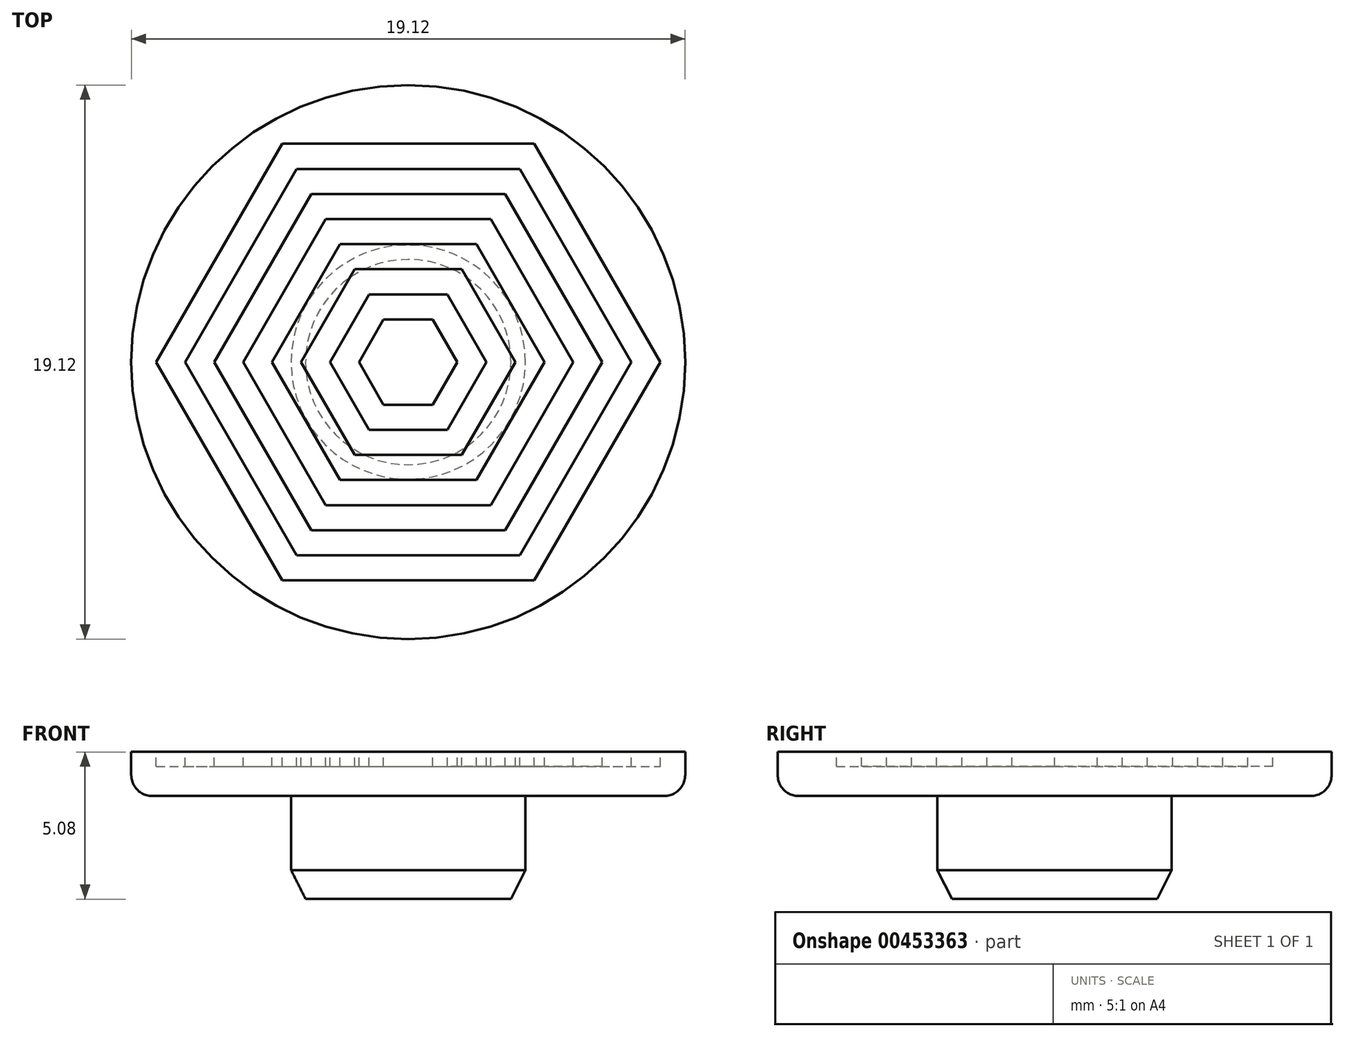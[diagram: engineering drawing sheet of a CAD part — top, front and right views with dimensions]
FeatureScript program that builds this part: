
annotation { "Feature Type Name" : "Feature", "Feature Type Description" : "" }
export const myFeature = defineFeature(function(context is Context, id is Id, definition is map)
    precondition{}
    {
        {
            var Q0;
            Q0=qCreatedBy(makeId("Top.planeOp"),FACE);
            var sketch = newSketch(context, id + "F0", { "sketchPlane" : qUnion([Q0])});
            skCircle(sketch, "E0", {"center": v(0, 0) * mm, "radius": 9.56 * mm});
            skSolve(sketch);
        }
        {
            var Q0;
            Q0=makeQuery(id+"F0.imprint","IMPRINT",FACE,{"disambiguationData":[TD([[makeQuery(id+"F0.imprint","IMPRINT",EDGE,{"derivedFrom":sQuery(id+"F0.wireOp",EDGE,"E0")}),1.0]])]});
            extrude(context, id + "F1", {"entities" : qUnion([Q0]), "depth" : 1.52 * mm});
        }
        {
            var Q0;
            Q0=makeQuery(id+"F1.opExtrude","CAP_FACE",FACE,{"disambiguationData":[OSD([sQuery(id+"F0.wireOp",EDGE,"E0")])],"isStart":false});
            var sketch = newSketch(context, id + "F2", { "sketchPlane" : qUnion([Q0])});
            skCircle(sketch, "E1.cCircle", {"center": v(0, 0) * mm, "radius": 2.34 * mm, "construction": true});
            skLineSegment(sketch, "E1.0", {"start": v(-1.35, 2.34) * mm, "end": v(1.35, 2.34) * mm});
            skLineSegment(sketch, "E1.1", {"start": v(1.35, 2.34) * mm, "end": v(2.7, 0) * mm});
            skLineSegment(sketch, "E1.2", {"start": v(2.7, 0) * mm, "end": v(1.35, -2.34) * mm});
            skLineSegment(sketch, "E1.3", {"start": v(1.35, -2.34) * mm, "end": v(-1.35, -2.34) * mm});
            skLineSegment(sketch, "E1.4", {"start": v(-1.35, -2.34) * mm, "end": v(-2.7, 0) * mm});
            skLineSegment(sketch, "E1.5", {"start": v(-2.7, 0) * mm, "end": v(-1.35, 2.34) * mm});
            skPoint(sketch, "E1.0.midPoint", {"position": v(0, 2.34) * mm});
            skCircle(sketch, "E2.cCircle", {"center": v(0, 0) * mm, "radius": 3.2 * mm, "construction": true});
            skLineSegment(sketch, "E2.0", {"start": v(-1.85, 3.2) * mm, "end": v(1.85, 3.2) * mm});
            skLineSegment(sketch, "E2.1", {"start": v(1.85, 3.2) * mm, "end": v(3.7, 0) * mm});
            skLineSegment(sketch, "E2.2", {"start": v(3.7, 0) * mm, "end": v(1.85, -3.2) * mm});
            skLineSegment(sketch, "E2.3", {"start": v(1.85, -3.2) * mm, "end": v(-1.85, -3.2) * mm});
            skLineSegment(sketch, "E2.4", {"start": v(-1.85, -3.2) * mm, "end": v(-3.7, 0) * mm});
            skLineSegment(sketch, "E2.5", {"start": v(-3.7, 0) * mm, "end": v(-1.85, 3.2) * mm});
            skPoint(sketch, "E2.0.midPoint", {"position": v(0, 3.2) * mm});
            skCircle(sketch, "E3.cCircle", {"center": v(0, 0) * mm, "radius": 1.47 * mm, "construction": true});
            skLineSegment(sketch, "E3.0", {"start": v(-0.85, 1.47) * mm, "end": v(0.85, 1.47) * mm});
            skLineSegment(sketch, "E3.1", {"start": v(0.85, 1.47) * mm, "end": v(1.7, 0) * mm});
            skLineSegment(sketch, "E3.2", {"start": v(1.7, 0) * mm, "end": v(0.85, -1.47) * mm});
            skLineSegment(sketch, "E3.3", {"start": v(0.85, -1.47) * mm, "end": v(-0.85, -1.47) * mm});
            skLineSegment(sketch, "E3.4", {"start": v(-0.85, -1.47) * mm, "end": v(-1.7, 0) * mm});
            skLineSegment(sketch, "E3.5", {"start": v(-1.7, 0) * mm, "end": v(-0.85, 1.47) * mm});
            skPoint(sketch, "E3.0.midPoint", {"position": v(0, 1.47) * mm});
            skCircle(sketch, "E4.cCircle", {"center": v(0, 0) * mm, "radius": 4.07 * mm, "construction": true});
            skLineSegment(sketch, "E4.0", {"start": v(-2.35, 4.07) * mm, "end": v(2.35, 4.07) * mm});
            skLineSegment(sketch, "E4.1", {"start": v(2.35, 4.07) * mm, "end": v(4.7, 0) * mm});
            skLineSegment(sketch, "E4.2", {"start": v(4.7, 0) * mm, "end": v(2.35, -4.07) * mm});
            skLineSegment(sketch, "E4.3", {"start": v(2.35, -4.07) * mm, "end": v(-2.35, -4.07) * mm});
            skLineSegment(sketch, "E4.4", {"start": v(-2.35, -4.07) * mm, "end": v(-4.7, 0) * mm});
            skLineSegment(sketch, "E4.5", {"start": v(-4.7, 0) * mm, "end": v(-2.35, 4.07) * mm});
            skPoint(sketch, "E4.0.midPoint", {"position": v(0, 4.07) * mm});
            skCircle(sketch, "E5.cCircle", {"center": v(0, 0) * mm, "radius": 4.94 * mm, "construction": true});
            skLineSegment(sketch, "E5.0", {"start": v(-2.85, 4.94) * mm, "end": v(2.85, 4.94) * mm});
            skLineSegment(sketch, "E5.1", {"start": v(2.85, 4.94) * mm, "end": v(5.7, 0) * mm});
            skLineSegment(sketch, "E5.2", {"start": v(5.7, 0) * mm, "end": v(2.85, -4.94) * mm});
            skLineSegment(sketch, "E5.3", {"start": v(2.85, -4.94) * mm, "end": v(-2.85, -4.94) * mm});
            skLineSegment(sketch, "E5.4", {"start": v(-2.85, -4.94) * mm, "end": v(-5.7, 0) * mm});
            skLineSegment(sketch, "E5.5", {"start": v(-5.7, 0) * mm, "end": v(-2.85, 4.94) * mm});
            skPoint(sketch, "E5.0.midPoint", {"position": v(0, 4.94) * mm});
            skCircle(sketch, "E6.cCircle", {"center": v(0, 0) * mm, "radius": 5.8 * mm, "construction": true});
            skLineSegment(sketch, "E6.0", {"start": v(-3.35, 5.8) * mm, "end": v(3.35, 5.8) * mm});
            skLineSegment(sketch, "E6.1", {"start": v(3.35, 5.8) * mm, "end": v(6.7, 0) * mm});
            skLineSegment(sketch, "E6.2", {"start": v(6.7, 0) * mm, "end": v(3.35, -5.8) * mm});
            skLineSegment(sketch, "E6.3", {"start": v(3.35, -5.8) * mm, "end": v(-3.35, -5.8) * mm});
            skLineSegment(sketch, "E6.4", {"start": v(-3.35, -5.8) * mm, "end": v(-6.7, 0) * mm});
            skLineSegment(sketch, "E6.5", {"start": v(-6.7, 0) * mm, "end": v(-3.35, 5.8) * mm});
            skPoint(sketch, "E6.0.midPoint", {"position": v(0, 5.8) * mm});
            skCircle(sketch, "E7.cCircle", {"center": v(0, 0) * mm, "radius": 6.67 * mm, "construction": true});
            skLineSegment(sketch, "E7.0", {"start": v(-3.85, 6.67) * mm, "end": v(3.85, 6.67) * mm});
            skLineSegment(sketch, "E7.1", {"start": v(3.85, 6.67) * mm, "end": v(7.7, 0) * mm});
            skLineSegment(sketch, "E7.2", {"start": v(7.7, 0) * mm, "end": v(3.85, -6.67) * mm});
            skLineSegment(sketch, "E7.3", {"start": v(3.85, -6.67) * mm, "end": v(-3.85, -6.67) * mm});
            skLineSegment(sketch, "E7.4", {"start": v(-3.85, -6.67) * mm, "end": v(-7.7, 0) * mm});
            skLineSegment(sketch, "E7.5", {"start": v(-7.7, 0) * mm, "end": v(-3.85, 6.67) * mm});
            skPoint(sketch, "E7.0.midPoint", {"position": v(0, 6.67) * mm});
            skCircle(sketch, "E8.cCircle", {"center": v(0, 0) * mm, "radius": 7.54 * mm, "construction": true});
            skLineSegment(sketch, "E8.0", {"start": v(4.35, 7.54) * mm, "end": v(8.7, 0) * mm});
            skLineSegment(sketch, "E8.1", {"start": v(8.7, 0) * mm, "end": v(4.35, -7.54) * mm});
            skLineSegment(sketch, "E8.2", {"start": v(4.35, -7.54) * mm, "end": v(-4.35, -7.54) * mm});
            skLineSegment(sketch, "E8.3", {"start": v(-4.35, -7.54) * mm, "end": v(-8.7, 0) * mm});
            skLineSegment(sketch, "E8.4", {"start": v(-8.7, 0) * mm, "end": v(-4.35, 7.54) * mm});
            skLineSegment(sketch, "E8.5", {"start": v(-4.35, 7.54) * mm, "end": v(4.35, 7.54) * mm});
            skPoint(sketch, "E8.0.midPoint", {"position": v(6.53, 3.77) * mm});
            skSolve(sketch);
        }
        {
            var Q0;
            Q0=makeQuery(id+"F2.imprint","IMPRINT",FACE,{"disambiguationData":[TD([[makeQuery(id+"F2.imprint","IMPRINT",EDGE,{"derivedFrom":sQuery(id+"F2.wireOp",EDGE,"E1.0")}),-1.0]])]});
            var Q1;
            Q1=makeQuery(id+"F2.imprint","IMPRINT",FACE,{"disambiguationData":[TD([[makeQuery(id+"F2.imprint","IMPRINT",EDGE,{"derivedFrom":sQuery(id+"F2.wireOp",EDGE,"E2.0")}),1.0]])]});
            var Q2;
            Q2=makeQuery(id+"F2.imprint","IMPRINT",FACE,{"disambiguationData":[TD([[makeQuery(id+"F2.imprint","IMPRINT",EDGE,{"derivedFrom":sQuery(id+"F2.wireOp",EDGE,"E5.0")}),1.0]])]});
            var Q3;
            Q3=makeQuery(id+"F2.imprint","IMPRINT",FACE,{"disambiguationData":[TD([[makeQuery(id+"F2.imprint","IMPRINT",EDGE,{"derivedFrom":sQuery(id+"F2.wireOp",EDGE,"E7.0")}),1.0]])]});
            extrude(context, id + "F3", {"entities" : qUnion([Q0, Q1, Q2, Q3]), "operationType" : NewBodyOperationType.REMOVE, "oppositeDirection" : true, "depth" : .5 * mm});
        }
        {
            var Q0;
            Q0=makeQuery(id+"F1.opExtrude","CAP_FACE",FACE,{"disambiguationData":[OSD([sQuery(id+"F0.wireOp",EDGE,"E0")])],"isStart":true});
            var sketch = newSketch(context, id + "F4", { "sketchPlane" : qUnion([Q0])});
            skCircle(sketch, "E9", {"center": v(0, 0) * mm, "radius": 4.04 * mm});
            skSolve(sketch);
        }
        {
            var Q0;
            Q0=makeQuery(id+"F4.imprint","IMPRINT",FACE,{"disambiguationData":[TD([[makeQuery(id+"F4.imprint","IMPRINT",EDGE,{"derivedFrom":sQuery(id+"F4.wireOp",EDGE,"E9")}),1.0]])]});
            extrude(context, id + "F5", {"entities" : qUnion([Q0]), "operationType" : NewBodyOperationType.ADD, "depth" : 3.56 * mm});
        }
        {
            var Q0;
            Q0=makeQuery(id+"F1.opExtrude","CAP_EDGE",EDGE,{"disambiguationData":[OSD([sQuery(id+"F0.wireOp",EDGE,"E0")])],"isStart":true});
            fillet(context, id + "F6", {"entities" : qUnion([Q0]), "radius" : 0.72 * mm, "tangentPropagation" : true, "allowEdgeOverflow" : false});
        }
        {
            var Q0;
            Q0=makeQuery(id+"F5.opExtrude","CAP_EDGE",EDGE,{"disambiguationData":[OSD([sQuery(id+"F4.wireOp",EDGE,"E9")])],"isStart":false});
            chamfer(context, id + "F7", {"entities" : qUnion([Q0]), "chamferType" : ChamferType.TWO_OFFSETS, "width1" : .5 * mm, "oppositeDirection" : false, "width2" : 1 * mm, "tangentPropagation" : true});
        }
    });
